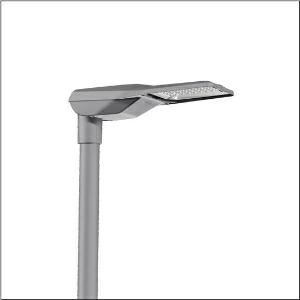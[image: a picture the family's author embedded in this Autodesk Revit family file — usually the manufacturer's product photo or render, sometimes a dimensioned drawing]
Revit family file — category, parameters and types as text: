
# Revit family: streetlight_sl_21_iq_mini___st1_0a_5xe2d31d08gb_54bd
name_source: partatom
category: Lighting Fixtures
units: mm (PartAtom-declared; Revit-internal decimal feet)

## family parameters
Cut with Voids When Loaded = No
Host = Face
Light Source = No
Part Type = Normal
Room Calculation Point = No
Round Connector Dimension = Use Diameter
Shared = No

## types (1)
- --- (1 x LED, 5680 lm, 37.1 W, 3000K)
    Apparent Load = 37 VA
    CIE Flux Codes = 37 72 97 100 100
    Color Rendering = 70
    Color Temperature = 3000K
    Default Elevation = 1800 mm
    Description = Streetlight SL 21 iQ mini, mast luminaire, primary light control with lens, of PMMA, primary optical cover: cover, of toughened safety glass, transparent, light distribution: ST1.0a, light emission: direct distribution, primary light characteristic: asymmetric, installation type: post-top, side-entry, LED, High Power LED, rated luminous flux: 5.680lm, luminous efficacy: 153lm/W, light colour: 730, colour temperature: 3000K, control: Auto-Match, Temp-Guard, Lumen-Switch, Night-Set, Smart-Wire, Light-Fading, Desk-Remote (wireless, voltage-free reading and setting of iQ features in the workshop via application-optimized NFC function/RFID function), optimised constant luminous flux control (CLO 2.0), presetting dimming linear, mains connection: 220..240V, AC, 50/60Hz, start of lifetime: 37W, end of service life: 39W, reduction: 18W, luminaire housing, of diecast aluminium, powder-coated, Siteco® metallic grey (DB 702S), corrosivity category C5 mid according to DIN EN ISO 12944, please order mast flange separately, inclination adjustable: 0°, 5°, 10°, 15°, sealing non-destructively replaceable, multi-level sealing system, length: 628mm, width: 235mm, height: 110mm, mast flange for spigot size: 42mm (side-entry): 5XC10008XM4, 60/48mm (side-entry/post-top): 5XC10108XM2, 76/60mm (side-entry/post-top): 5XC10108XM1, protection rating (complete): IP66, insulation class (complete): insulation class II (safety insulation), certification: CE, ENEC, ENEC+, VDE, impact resistance: IK09, permissible operating ambient temperature for outdoor applications: -40..+50°C, standard-compliant lighting for roads and squares, packaging unit: 1 piece

Light Distribution: ST1.0a
    Height = 110 mm
    Lamp = 1 x LED
    Lamp Light Flux = 5680 lm
    Lamp Power = 37.1 W
    Lamp count = 1
    Length = 625 mm
    Luminous efficacy = 153 lm/W
    Manufacturer = Siteco
    ModVariant = No
    Model = 5XE2D31D08GB
    Number of Poles = 1
    OnlyDefault = Yes
    Power Factor = 1
    Product Name = Streetlight SL 21 iQ mini | ST1.0a
    Product group = mast luminaire | pylon top
    ProductGroupID = 6100
    Protection Class = Protection class II
    Protection Degree = IP 66
    RLX_Detail_Level = 1
    RLX_Emergency_Light_Flux = 0 lm
    RLX_Emergency_Type = 0
    RLX_Emergency_Type_DB = No
    RlxData = <blob elided: 92301 chars, md5=26906fba>
    Socket = socket
    Standby Power = 0 W
    System Light Flux = 5680 lm
    System Power = 37 W
    Type Comments = factory setting: luminous flux: 100 % | dim-lin: 254 | 385 mA
    Type Image = l_1003519.jpg
    URL = http://relux.com
    VarID = @adj_141013
    Voltage = 0 V
    Weight = 0.00 kg
    Width = 234 mm

## geometry (parser evidence)
native form markers: Blend x4, Sweep x10
no freeform markers — native parametric forms only
